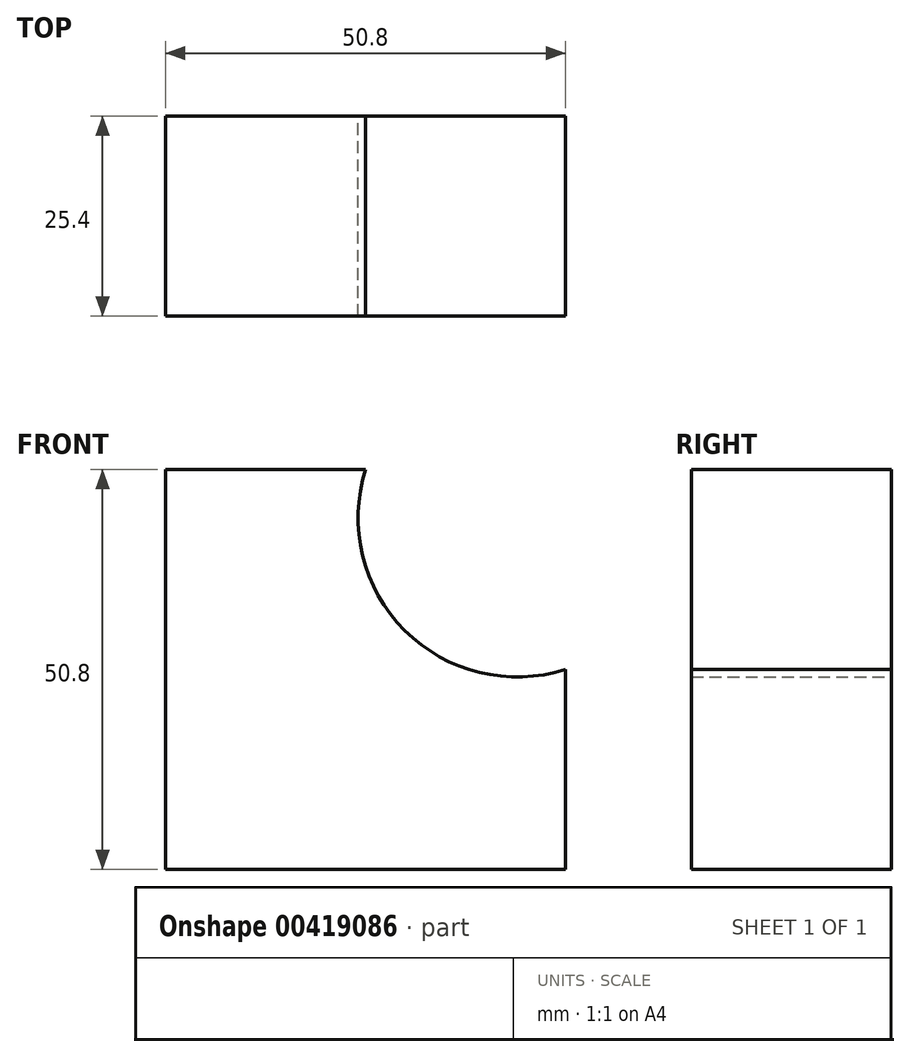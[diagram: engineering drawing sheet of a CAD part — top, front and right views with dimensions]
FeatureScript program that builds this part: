
annotation { "Feature Type Name" : "Feature", "Feature Type Description" : "" }
export const myFeature = defineFeature(function(context is Context, id is Id, definition is map)
    precondition{}
    {
        {
            var Q0;
            Q0=qCreatedBy(makeId("Front.planeOp"),FACE);
            var sketch = newSketch(context, id + "F0", { "sketchPlane" : qUnion([Q0])});
            skLineSegment(sketch, "E0", {"start": v(0, 0) * mm, "end": v(-50.8, 0) * mm});
            skLineSegment(sketch, "E1", {"start": v(-50.8, 0) * mm, "end": v(-50.8, 50.8) * mm});
            skLineSegment(sketch, "E2", {"start": v(-50.8, 50.8) * mm, "end": v(-25.4, 50.8) * mm});
            skLineSegment(sketch, "E3", {"start": v(0, 0) * mm, "end": v(0, 25.4) * mm});
            skArc(sketch, "E4", {"start": v(-25.4, 50.8) * mm, "mid": v(-20.43, 30.37) * mm, "end": v(0, 25.4) * mm});
            skSolve(sketch);
        }
        {
            var Q0;
            Q0=makeQuery(id+"F0.imprint","IMPRINT",FACE,{"disambiguationData":[TD([[makeQuery(id+"F0.imprint","IMPRINT",EDGE,{"derivedFrom":sQuery(id+"F0.wireOp",EDGE,"E0")}),-1.0]])]});
            extrude(context, id + "F1", {"entities" : qUnion([Q0]), "depth" : 25.4 * mm});
        }
    });
